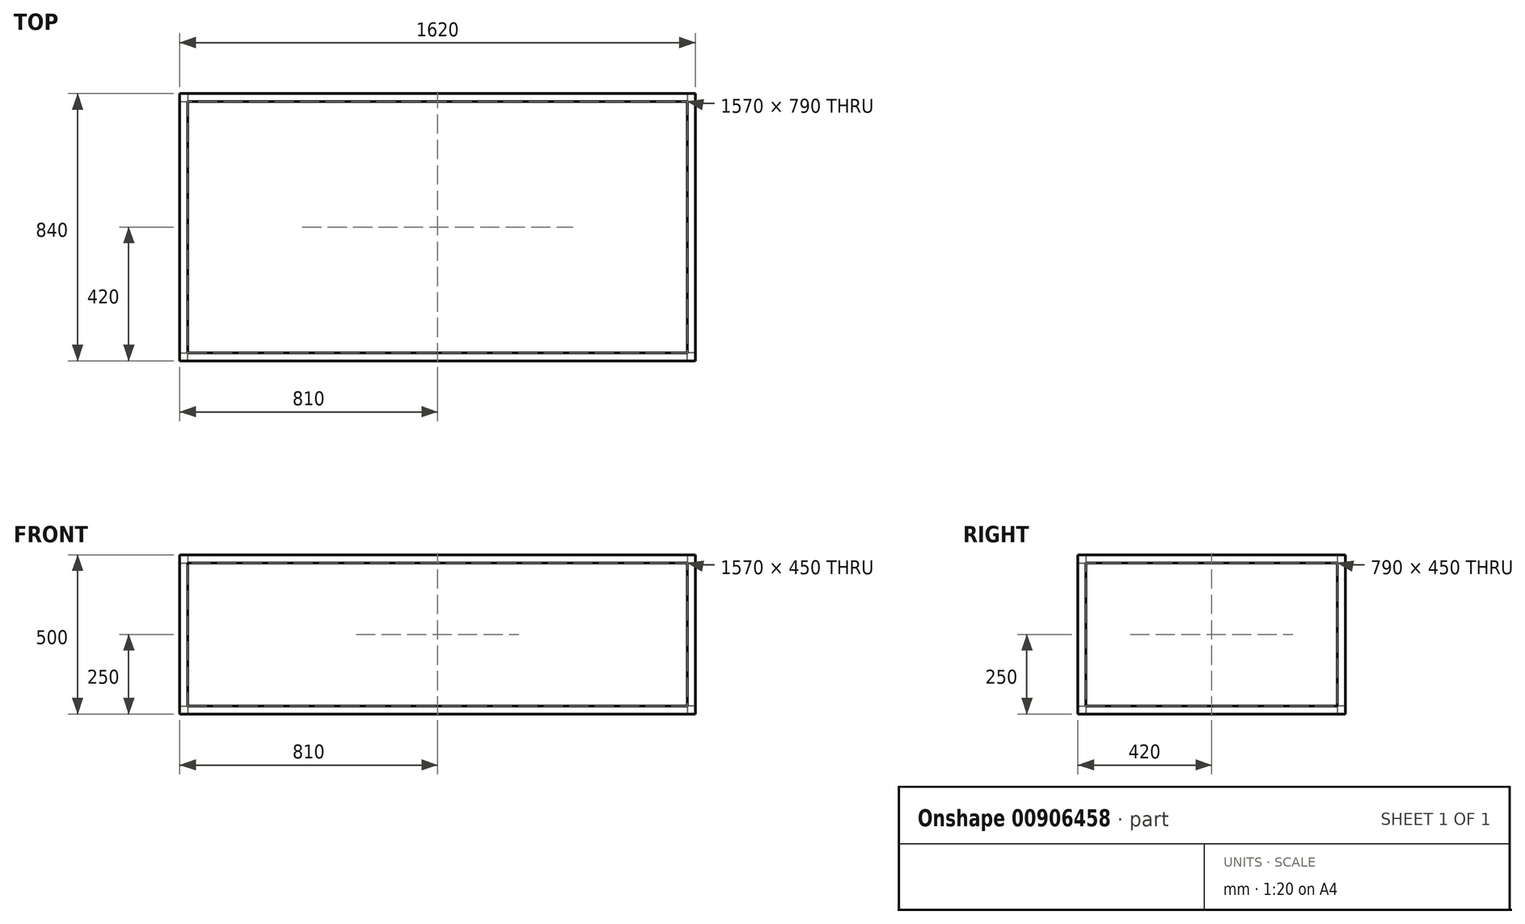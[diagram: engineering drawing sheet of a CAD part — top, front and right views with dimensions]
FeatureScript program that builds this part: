
annotation { "Feature Type Name" : "Feature", "Feature Type Description" : "" }
export const myFeature = defineFeature(function(context is Context, id is Id, definition is map)
    precondition{}
    {
        {
            var Q0;
            Q0=qCreatedBy(makeId("Top.planeOp"),FACE);
            var sketch = newSketch(context, id + "F0", { "sketchPlane" : qUnion([Q0])});
            skLineSegment(sketch, "E0.bottom", {"start": v(0, 0) * mm, "end": v(-1620, 0) * mm});
            skLineSegment(sketch, "E0.top", {"start": v(0, 840) * mm, "end": v(-1620, 840) * mm});
            skLineSegment(sketch, "E0.left", {"start": v(0, 0) * mm, "end": v(0, 840) * mm});
            skLineSegment(sketch, "E0.right", {"start": v(-1620, 0) * mm, "end": v(-1620, 840) * mm});
            skLineSegment(sketch, "E1.top", {"start": v(-1595, 815) * mm, "end": v(-810, 815) * mm});
            skLineSegment(sketch, "E1.left", {"start": v(-1595, 420) * mm, "end": v(-1595, 815) * mm});
            skLineSegment(sketch, "E2.top", {"start": v(-1595, 25) * mm, "end": v(-810, 25) * mm});
            skLineSegment(sketch, "E2.left", {"start": v(-1595, 420) * mm, "end": v(-1595, 25) * mm});
            skLineSegment(sketch, "E3.bottom", {"start": v(-810, 25) * mm, "end": v(-25, 25) * mm});
            skLineSegment(sketch, "E3.right", {"start": v(-25, 25) * mm, "end": v(-25, 420) * mm});
            skLineSegment(sketch, "E4.bottom", {"start": v(-810, 815) * mm, "end": v(-25, 815) * mm});
            skLineSegment(sketch, "E4.right", {"start": v(-25, 815) * mm, "end": v(-25, 420) * mm});
            skLineSegment(sketch, "E5", {"start": v(-1595, 815) * mm, "end": v(-1620, 840) * mm});
            skLineSegment(sketch, "E6", {"start": v(-25, 815) * mm, "end": v(0, 840) * mm});
            skLineSegment(sketch, "E7", {"start": v(-1595, 25) * mm, "end": v(-1620, 0) * mm});
            skLineSegment(sketch, "E8", {"start": v(-25, 25) * mm, "end": v(0, 0) * mm});
            skSolve(sketch);
        }
        {
            var Q0;
            Q0 = qSketchRegion(id + "F0", true);
            extrude(context, id + "F1", {"entities" : qUnion([Q0]), "depth" : 25 * mm, "offsetDistance" : 25 * mm});
        }
        {
            var Q0;
            Q0=makeQuery(id+"F1.opExtrude","CAP_FACE",FACE,{"disambiguationData":[OSD([sQuery(id+"F0.wireOp",EDGE,"E0.bottom"),sQuery(id+"F0.wireOp",EDGE,"E0.top"),sQuery(id+"F0.wireOp",EDGE,"E0.left"),sQuery(id+"F0.wireOp",EDGE,"E0.right"),sQuery(id+"F0.wireOp",EDGE,"E1.top"),sQuery(id+"F0.wireOp",EDGE,"E1.left"),sQuery(id+"F0.wireOp",EDGE,"E2.top"),sQuery(id+"F0.wireOp",EDGE,"E2.left"),sQuery(id+"F0.wireOp",EDGE,"E3.bottom"),sQuery(id+"F0.wireOp",EDGE,"E3.right"),sQuery(id+"F0.wireOp",EDGE,"E4.bottom"),sQuery(id+"F0.wireOp",EDGE,"E4.right")])],"isStart":false});
            var sketch = newSketch(context, id + "F2", { "sketchPlane" : qUnion([Q0])});
            skLineSegment(sketch, "E9.bottom", {"start": v(-1620, 0) * mm, "end": v(-1595, 0) * mm});
            skLineSegment(sketch, "E9.top", {"start": v(-1620, 25) * mm, "end": v(-1595, 25) * mm});
            skLineSegment(sketch, "E9.left", {"start": v(-1620, 0) * mm, "end": v(-1620, 25) * mm});
            skLineSegment(sketch, "E9.right", {"start": v(-1595, 0) * mm, "end": v(-1595, 25) * mm});
            skLineSegment(sketch, "E10.bottom", {"start": v(-1620, 840) * mm, "end": v(-1595, 840) * mm});
            skLineSegment(sketch, "E10.top", {"start": v(-1620, 815) * mm, "end": v(-1595, 815) * mm});
            skLineSegment(sketch, "E10.left", {"start": v(-1620, 840) * mm, "end": v(-1620, 815) * mm});
            skLineSegment(sketch, "E10.right", {"start": v(-1595, 840) * mm, "end": v(-1595, 815) * mm});
            skLineSegment(sketch, "E11.bottom", {"start": v(0, 840) * mm, "end": v(-25, 840) * mm});
            skLineSegment(sketch, "E11.top", {"start": v(0, 815) * mm, "end": v(-25, 815) * mm});
            skLineSegment(sketch, "E11.left", {"start": v(0, 840) * mm, "end": v(0, 815) * mm});
            skLineSegment(sketch, "E11.right", {"start": v(-25, 840) * mm, "end": v(-25, 815) * mm});
            skLineSegment(sketch, "E12.bottom", {"start": v(0, 0) * mm, "end": v(-25, 0) * mm});
            skLineSegment(sketch, "E12.top", {"start": v(0, 25) * mm, "end": v(-25, 25) * mm});
            skLineSegment(sketch, "E12.left", {"start": v(0, 0) * mm, "end": v(0, 25) * mm});
            skLineSegment(sketch, "E12.right", {"start": v(-25, 0) * mm, "end": v(-25, 25) * mm});
            skSolve(sketch);
        }
        {
            var Q0;
            Q0=makeQuery(id+"F2.imprint","IMPRINT",FACE,{"disambiguationData":[TD([[makeQuery(id+"F2.imprint","IMPRINT",EDGE,{"derivedFrom":sQuery(id+"F2.wireOp",EDGE,"E9.bottom")}),-1.0]])]});
            var Q1;
            Q1=makeQuery(id+"F2.imprint","IMPRINT",FACE,{"disambiguationData":[TD([[makeQuery(id+"F2.imprint","IMPRINT",EDGE,{"derivedFrom":sQuery(id+"F2.wireOp",EDGE,"E10.bottom")}),1.0]])]});
            var Q2;
            Q2=makeQuery(id+"F2.imprint","IMPRINT",FACE,{"disambiguationData":[TD([[makeQuery(id+"F2.imprint","IMPRINT",EDGE,{"derivedFrom":sQuery(id+"F2.wireOp",EDGE,"E12.bottom")}),-1.0]])]});
            var Q3;
            Q3=makeQuery(id+"F2.imprint","IMPRINT",FACE,{"disambiguationData":[TD([[makeQuery(id+"F2.imprint","IMPRINT",EDGE,{"derivedFrom":sQuery(id+"F2.wireOp",EDGE,"E11.bottom")}),1.0]])]});
            extrude(context, id + "F3", {"entities" : qUnion([Q0, Q1, Q2, Q3]), "operationType" : NewBodyOperationType.ADD, "depth" : 450 * mm, "offsetDistance" : 25 * mm});
        }
        {
            var Q0;
            Q0=makeQuery(id+"F3.opExtrude","CAP_FACE",FACE,{"disambiguationData":[OSD([sQuery(id+"F2.wireOp",EDGE,"E11.bottom"),sQuery(id+"F2.wireOp",EDGE,"E11.top"),sQuery(id+"F2.wireOp",EDGE,"E11.left"),sQuery(id+"F2.wireOp",EDGE,"E11.right")])],"isStart":false});
            var sketch = newSketch(context, id + "F4", { "sketchPlane" : qUnion([Q0])});
            skLineSegment(sketch, "E13.bottom", {"start": v(0, 840) * mm, "end": v(-1620, 840) * mm});
            skLineSegment(sketch, "E13.top", {"start": v(0, 0) * mm, "end": v(-1620, 0) * mm});
            skLineSegment(sketch, "E13.left", {"start": v(0, 840) * mm, "end": v(0, 0) * mm});
            skLineSegment(sketch, "E13.right", {"start": v(-1620, 840) * mm, "end": v(-1620, 0) * mm});
            skLineSegment(sketch, "E14.top", {"start": v(-1595, 815) * mm, "end": v(-810, 815) * mm});
            skLineSegment(sketch, "E14.left", {"start": v(-1595, 420) * mm, "end": v(-1595, 815) * mm});
            skLineSegment(sketch, "E15.bottom", {"start": v(-810, 25) * mm, "end": v(-25, 25) * mm});
            skLineSegment(sketch, "E15.right", {"start": v(-25, 25) * mm, "end": v(-25, 420) * mm});
            skLineSegment(sketch, "E16.bottom", {"start": v(-810, 25) * mm, "end": v(-1595, 25) * mm});
            skLineSegment(sketch, "E16.right", {"start": v(-1595, 25) * mm, "end": v(-1595, 420) * mm});
            skLineSegment(sketch, "E17.top", {"start": v(-25, 815) * mm, "end": v(-810, 815) * mm});
            skLineSegment(sketch, "E17.left", {"start": v(-25, 420) * mm, "end": v(-25, 815) * mm});
            skLineSegment(sketch, "E18", {"start": v(0, 0) * mm, "end": v(-25, 25) * mm});
            skLineSegment(sketch, "E19", {"start": v(0, 840) * mm, "end": v(-25, 815) * mm});
            skLineSegment(sketch, "E20", {"start": v(-1620, 840) * mm, "end": v(-1595, 815) * mm});
            skLineSegment(sketch, "E21", {"start": v(-1620, 0) * mm, "end": v(-1595, 25) * mm});
            skSolve(sketch);
        }
        {
            var Q0;
            Q0 = qSketchRegion(id + "F4", true);
            extrude(context, id + "F5", {"entities" : qUnion([Q0]), "operationType" : NewBodyOperationType.ADD, "depth" : 25 * mm, "offsetDistance" : 25 * mm});
        }
    });
